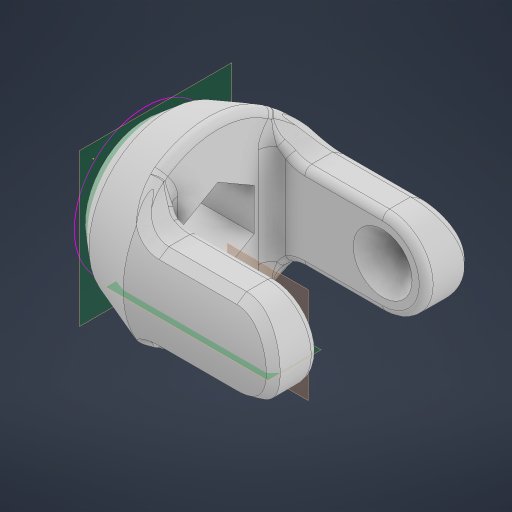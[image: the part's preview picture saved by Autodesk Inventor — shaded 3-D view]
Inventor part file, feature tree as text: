
AUTODESK INVENTOR PART (.ipt)
format: ipt  version: 2024 (Build 280153000, 153)  size: 643,584 bytes
history: native  units: in
note: dims shown in document units (in); Inventor stores cm internally (conversion verified against a paired STEP export)
features: sketch x6, extrude x4, fillet x4, projected_geometry x4, other x4, plane x3, chamfer x3, reference x2, revolve x1, mirror x1
ambient origin geometry x8: Origin, YZ Plane, XZ Plane, XY Plane, X Axis, Y Axis, Z Axis, Center Point
bodies: Solid1 (feature_tree)
feature tree (32):
  plane  "Work Plane2"
  extrude  "Extrusion1"  Depth=0.6299in
  plane  "Work Plane3"
  revolve  "Revolution1"  [1 undecoded]
  extrude  "Extrusion2"  TaperAngle=45.0deg  [1 undecoded]
  extrude  "Extrusion3"  Depth=0.4134in TaperAngle=0.0deg
  chamfer  "Chamfer1"  Distance=0.4134in
  fillet  "Fillet1"  Radius=0.1875in
  chamfer  "Chamfer2"  Distance=0.0394in
  mirror  "Mirror1"
  sketch  "Sketch7"  dims[d12=0.4375in d13=0.125in d14=0.1374in d15=0.1875in d16=0.0394in d17=0.125in d18=0.1374in d19=0.6693in]
  fillet  "Fillet4"  Radius=0.6693in
  plane  "Work Plane4"
  chamfer  "Chamfer3"  Distance=0.063in
  fillet  "Fillet5"  Radius=0.0394in
  fillet  "Fillet6"  Radius=0.0394in
  extrude  "Extrusion6"  Depth=0.4134in
  sketch  "Sketch2"  dims[d0=0.0118in d1=0.6299in]
  reference  "Reference14"
  sketch  "Sketch3"  dims[d2=0.6299in d3=0.2559in d4=0.0in]
  projected_geometry  "Projected Loop1"
  sketch  "Sketch4"  dims[d5=0.1673in d6=45.0deg]
  projected_geometry  "Projected Loop2"
  reference  "Reference15"
  sketch  "Sketch6"  dims[d7=90.0deg d8=1.1309in d9=0.0in d10=0.4134in d11=0.0in]
  projected_geometry  "Projected Loop3"
  sketch  "Sketch10"  dims[d22=0.0787in d26=0.063in d27=0.125in d28=0.3436in d29=0.0394in d30=0.0394in d38=0.4134in d39=0.4134in d40=0.0in]
  projected_geometry  "Projected Loop6"
  other  "<userpath>\Desktop\SeniorDesign\Universal_Joint.iam"
  other  "Universal_Joint.iam"
  other  "Universal_Joint:1"
  other  "Assembly2"
note: 2 required parameter values undecoded (feature->parameter linkage not recoverable at this tier; creation-order binding heuristic only, values carry confidence <= 0.55)